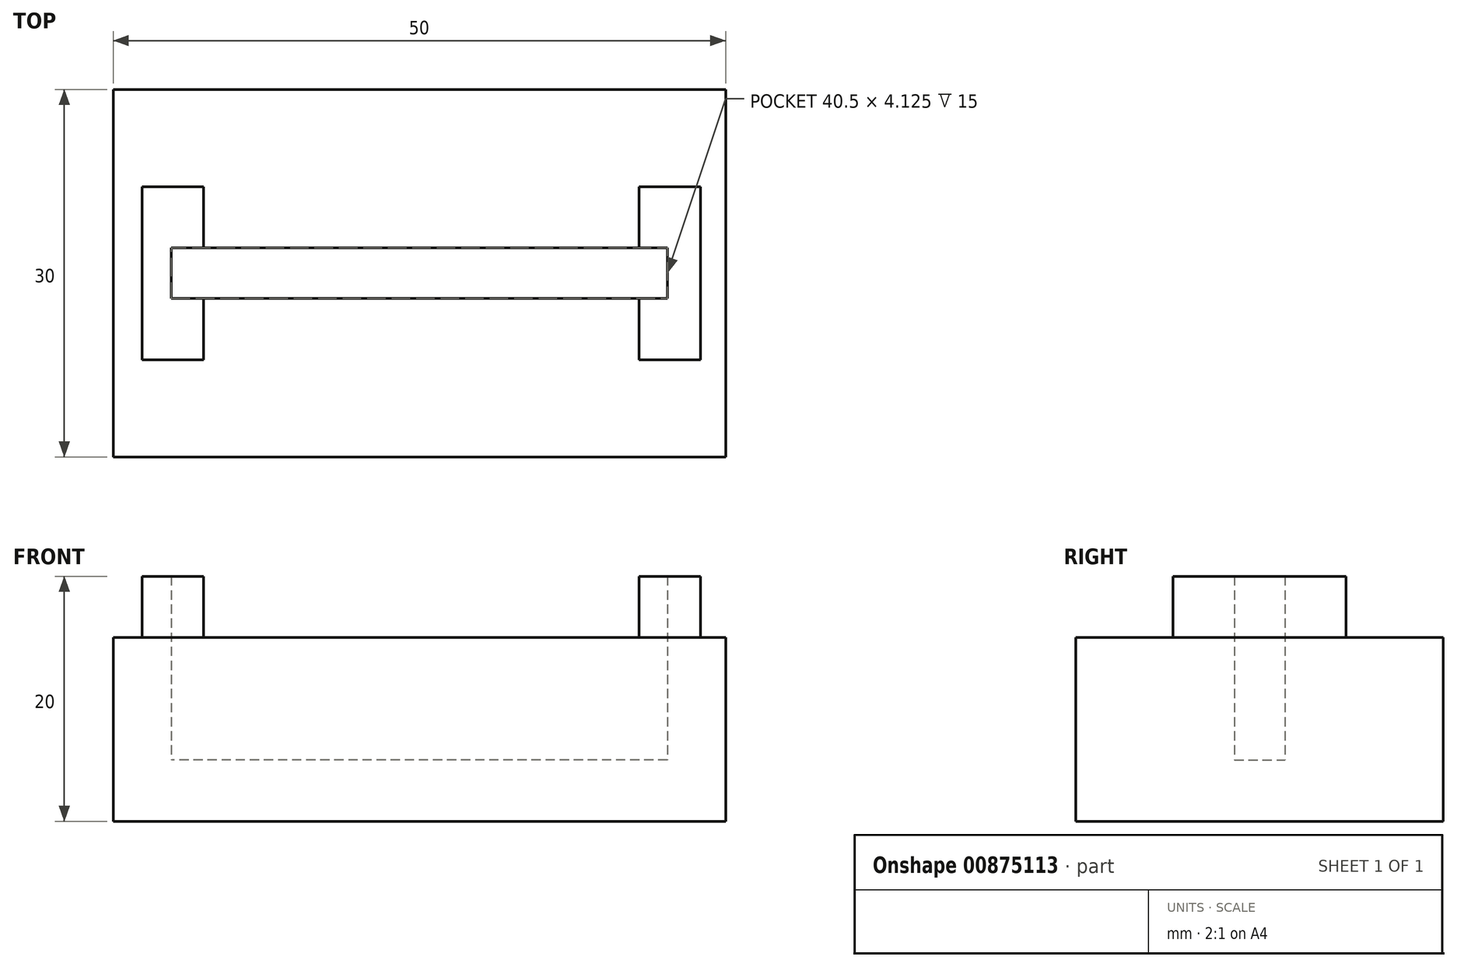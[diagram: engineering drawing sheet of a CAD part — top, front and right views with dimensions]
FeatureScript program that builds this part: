
annotation { "Feature Type Name" : "Feature", "Feature Type Description" : "" }
export const myFeature = defineFeature(function(context is Context, id is Id, definition is map)
    precondition{}
    {
        {
            var Q0;
            Q0=qCreatedBy(makeId("Top.planeOp"),FACE);
            var sketch = newSketch(context, id + "F0", { "sketchPlane" : qUnion([Q0])});
            skLineSegment(sketch, "E0.bottom", {"start": v(25, -15) * mm, "end": v(-25, -15) * mm});
            skLineSegment(sketch, "E0.top", {"start": v(25, 15) * mm, "end": v(-25, 15) * mm});
            skLineSegment(sketch, "E0.left", {"start": v(25, -15) * mm, "end": v(25, 15) * mm});
            skLineSegment(sketch, "E0.right", {"start": v(-25, -15) * mm, "end": v(-25, 15) * mm});
            skPoint(sketch, "E0.middle", {"position": v(0, 0) * mm});
            skLineSegment(sketch, "E1.bottom", {"start": v(20.25, -2.06) * mm, "end": v(-20.25, -2.06) * mm});
            skLineSegment(sketch, "E1.top", {"start": v(20.25, 2.06) * mm, "end": v(-20.25, 2.06) * mm});
            skLineSegment(sketch, "E1.left", {"start": v(20.25, -2.06) * mm, "end": v(20.25, 2.06) * mm});
            skLineSegment(sketch, "E1.right", {"start": v(-20.25, -2.06) * mm, "end": v(-20.25, 2.06) * mm});
            skLineSegment(sketch, "E2", {"start": v(-17.64, 2.06) * mm, "end": v(-17.64, 7.06) * mm});
            skLineSegment(sketch, "E3", {"start": v(-17.64, 7.06) * mm, "end": v(-22.64, 7.06) * mm});
            skLineSegment(sketch, "E4", {"start": v(-22.64, 7.06) * mm, "end": v(-22.64, -7.06) * mm});
            skLineSegment(sketch, "E5", {"start": v(-22.64, -7.06) * mm, "end": v(-17.64, -7.06) * mm});
            skLineSegment(sketch, "E6", {"start": v(-17.64, -7.06) * mm, "end": v(-17.64, -2.06) * mm});
            skLineSegment(sketch, "E7", {"start": v(17.93, 2.06) * mm, "end": v(17.93, 7.06) * mm});
            skLineSegment(sketch, "E8", {"start": v(17.93, 7.06) * mm, "end": v(22.93, 7.06) * mm});
            skLineSegment(sketch, "E9", {"start": v(22.93, 7.06) * mm, "end": v(22.93, -7.06) * mm});
            skLineSegment(sketch, "E10", {"start": v(22.93, -7.06) * mm, "end": v(17.93, -7.06) * mm});
            skLineSegment(sketch, "E11", {"start": v(17.93, -7.06) * mm, "end": v(17.93, -2.06) * mm});
            skSolve(sketch);
        }
        {
            var Q0;
            {var subQ0=sQuery(id+"F0.wireOp",EDGE,"E1.left");Q0=makeQuery(id+"F0.imprint","IMPRINT",FACE,{"disambiguationData":[TD([[makeQuery(id+"F0.imprint","IMPRINT",EDGE,{"derivedFrom":subQ0}),1.0]])]});}
            extrude(context, id + "F1", {"entities" : qUnion([Q0]), "depth" : 5 * mm, "offsetDistance" : 25 * mm});
        }
        {
            var Q0;
            Q0=makeQuery(id+"F0.imprint","IMPRINT",FACE,{"disambiguationData":[TD([[makeQuery(id+"F0.imprint","IMPRINT",EDGE,{"derivedFrom":sQuery(id+"F0.wireOp",EDGE,"E0.bottom")}),-1.0]])]});
            extrude(context, id + "F2", {"entities" : qUnion([Q0]), "operationType" : NewBodyOperationType.ADD, "depth" : 15 * mm, "offsetDistance" : 25 * mm});
        }
        {
            var Q0;
            {var subQ1=sQuery(id+"F0.wireOp",EDGE,"E1.right");Q0=makeQuery(id+"F0.imprint","IMPRINT",FACE,{"disambiguationData":[TD([[makeQuery(id+"F0.imprint","IMPRINT",EDGE,{"derivedFrom":subQ1}),1.0]])]});}
            var Q1;
            {var subQ0=sQuery(id+"F0.wireOp",EDGE,"E1.left");Q1=makeQuery(id+"F0.imprint","IMPRINT",FACE,{"disambiguationData":[TD([[makeQuery(id+"F0.imprint","IMPRINT",EDGE,{"derivedFrom":subQ0}),-1.0]])]});}
            extrude(context, id + "F3", {"entities" : qUnion([Q0, Q1]), "operationType" : NewBodyOperationType.ADD, "depth" : 20 * mm, "offsetDistance" : 25 * mm});
        }
    });
